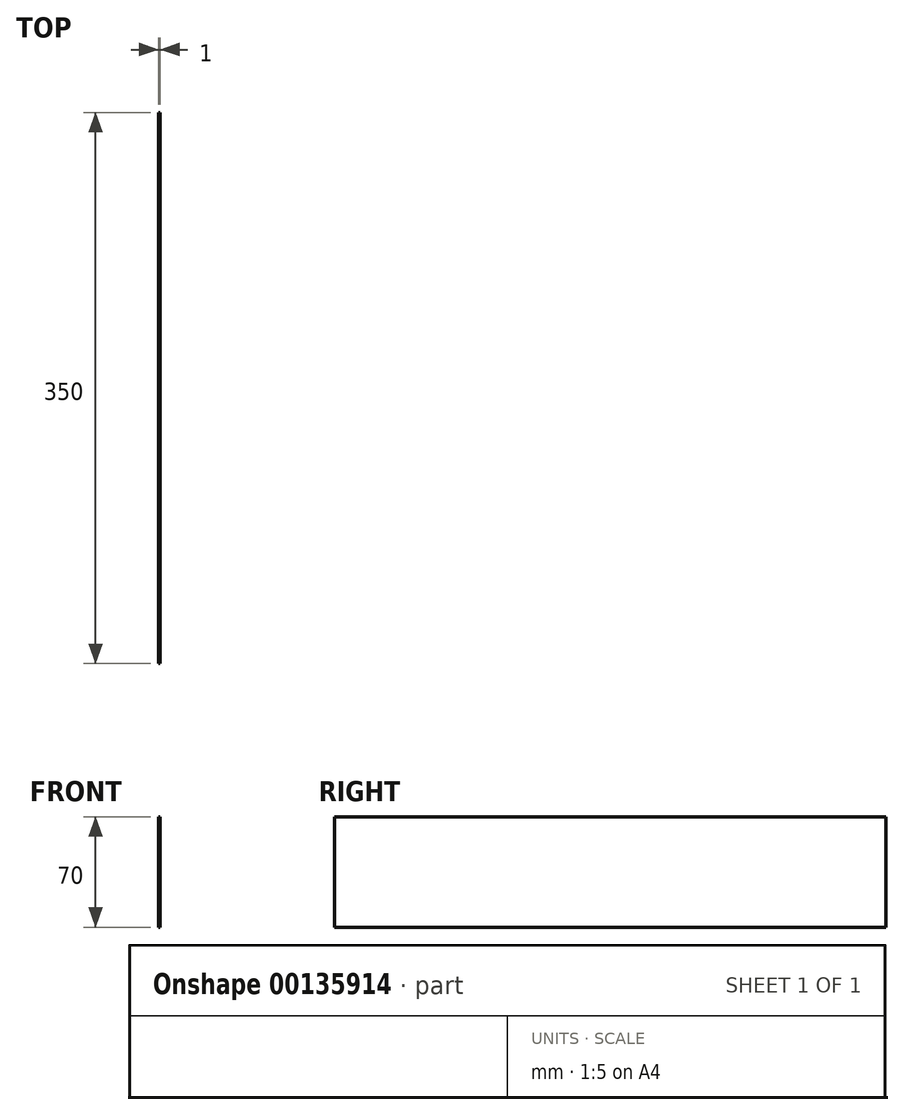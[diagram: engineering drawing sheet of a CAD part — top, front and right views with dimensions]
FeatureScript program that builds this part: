
annotation { "Feature Type Name" : "Feature", "Feature Type Description" : "" }
export const myFeature = defineFeature(function(context is Context, id is Id, definition is map)
    precondition{}
    {
        {
            var Q0;
            Q0=qCreatedBy(makeId("Right.planeOp"),FACE);
            var sketch = newSketch(context, id + "F0", { "sketchPlane" : qUnion([Q0])});
            skLineSegment(sketch, "E0.bottom", {"start": v(0, 0) * mm, "end": v(350, 0) * mm});
            skLineSegment(sketch, "E0.top", {"start": v(0, 70) * mm, "end": v(350, 70) * mm});
            skLineSegment(sketch, "E0.left", {"start": v(0, 0) * mm, "end": v(0, 70) * mm});
            skLineSegment(sketch, "E0.right", {"start": v(350, 0) * mm, "end": v(350, 70) * mm});
            skSolve(sketch);
        }
        {
            var Q0;
            Q0 = qSketchRegion(id + "F0", true);
            extrude(context, id + "F1", {"entities" : qUnion([Q0]), "depth" : 1 * mm});
        }
    });
